# Revit family: streetlight_sl_11_iq_micro___st1_2a_5xc1a61g08de_0f1d
name_source: partatom
category: Lighting Fixtures
units: mm (PartAtom-declared; Revit-internal decimal feet)

## family parameters
Cut with Voids When Loaded = No
Host = Face
Light Source = No
Part Type = Normal
Room Calculation Point = No
Round Connector Dimension = Use Diameter
Shared = No

## types (1)
- --- (1 x LED, 3320 lm, 25.6 W, 2700K)
    Apparent Load = 26 VA
    CIE Flux Codes = 33 71 96 100 100
    Color Rendering = 70
    Color Temperature = 2700K
    Default Elevation = 1800 mm
    Description = Streetlight SL 11 iQ micro, mast luminaire, primary light control with 3 zone facetted reflector, of plastic, silver coated, highly specular, primary optical cover: cover, of PMMA, transparent, light distribution: ST1.2a, light emission: direct distribution, primary light characteristic: asymmetric, installation type: side-entry, post-top, lamps: LED, High Power LED, rated values: 3.320lm | 25,6W | 129,7lm/W (begin service life); end service life: 3.320lm | 26,3W; at 50% lumin. flux: 1.660lm | 12,4W | 133,9lm/W, colour temperature: 2700K, colour rendering: CRI > 70, light colour: 727, light setting 1 begin service life: 100% | 3.320lm | 25,6W | 129,7lm/W | 2.700K, light setting 1 end service life: 26,3W, further light settings possible, control: optimised constant luminous flux control (CLO 2.0), Desk-Remote (wireless, voltage-free reading and setting of iQ features in the workshop via application-optimized NFC function/RFID function), Light-Fading, Smart-Wire, Night-Set, Lumen-Switch, Temp-Guard, Auto-Match, Street-Remote, pre-setting: linear dimming characteristic, with cable H07RN-F 5x 1.5mm², mains connection: 230..240V, AC, 50/60Hz, connection cable pre-assembled, cable length: 6,5m, luminaire housing, of diecast aluminium, powder-coated, SITECO metallic grey (DB 702S), please order mast flange separately, inclination adjustable without tools: 0°, 5°, 10°, 15° (post-top) | 0°, -5°, -10°, -15° (side-entry), sealing non-destructively replaceable, multi-level sealing system, length: 600mm, width: 174mm, height: 116mm, mast flange for spigot size: 42mm (side-entry): 5XC10008XM4, 60/48mm (side-entry/post-top): 5XC10108XM2, 76/60mm (side-entry/post-top): 5XC10108XM1, equipment: Power, protection rating (complete): IP66, insulation class (complete): insulation class II (safety insulation), certification: CE, ENEC, ENEC+, VDE, impact resistance: IK10, permissible operating ambient temperature for outdoor applications: -25..+50°C, standard-compliant lighting for roads and squares, Environmental Product Declaration (EPD) tested and certified by an independent institute, packaging unit: 1 piece

Light Distribution: ST1.2a
    Height = 116 mm
    Lamp = 1 x LED
    Lamp Light Flux = 3320 lm
    Lamp Power = 25.6 W
    Lamp count = 1
    Length = 600 mm
    Luminous efficacy = 130 lm/W
    Manufacturer = Siteco
    ModVariant = No
    Model = 5XC1A61G08DE
    Mounting Place = Pole
    Mounting Type = Pole top
    Number of Poles = 1
    OnlyDefault = Yes
    Power Factor = 1
    Product Name = Streetlight SL 11 iQ micro | ST1.2a
    Product group = mast luminaire | pylon top
    ProductGroupID = 6100
    Protection Class = Protection class II
    Protection Degree = IP 66
    RLX_Detail_Level = 1
    RLX_Emergency_Light_Flux = 0 lm
    RLX_Emergency_Type = 0
    RLX_Emergency_Type_DB = No
    RlxData = <blob elided: 50221 chars, md5=2c6731f9>
    Socket = socket
    Standby Power = 0 W
    System Light Flux = 3320 lm
    System Power = 26 W
    Type Comments = factory setting: luminous flux: 100 % | dim-lin: 254 | 478 mA
    Type Image = l_1006566.jpg
    URL = http://relux.com
    VarID = @adj_088001
    Voltage = 0 V
    Weight = 0.00 kg
    Width = 174 mm

## geometry (parser evidence)
native form markers: Sweep x9
no freeform markers — native parametric forms only
